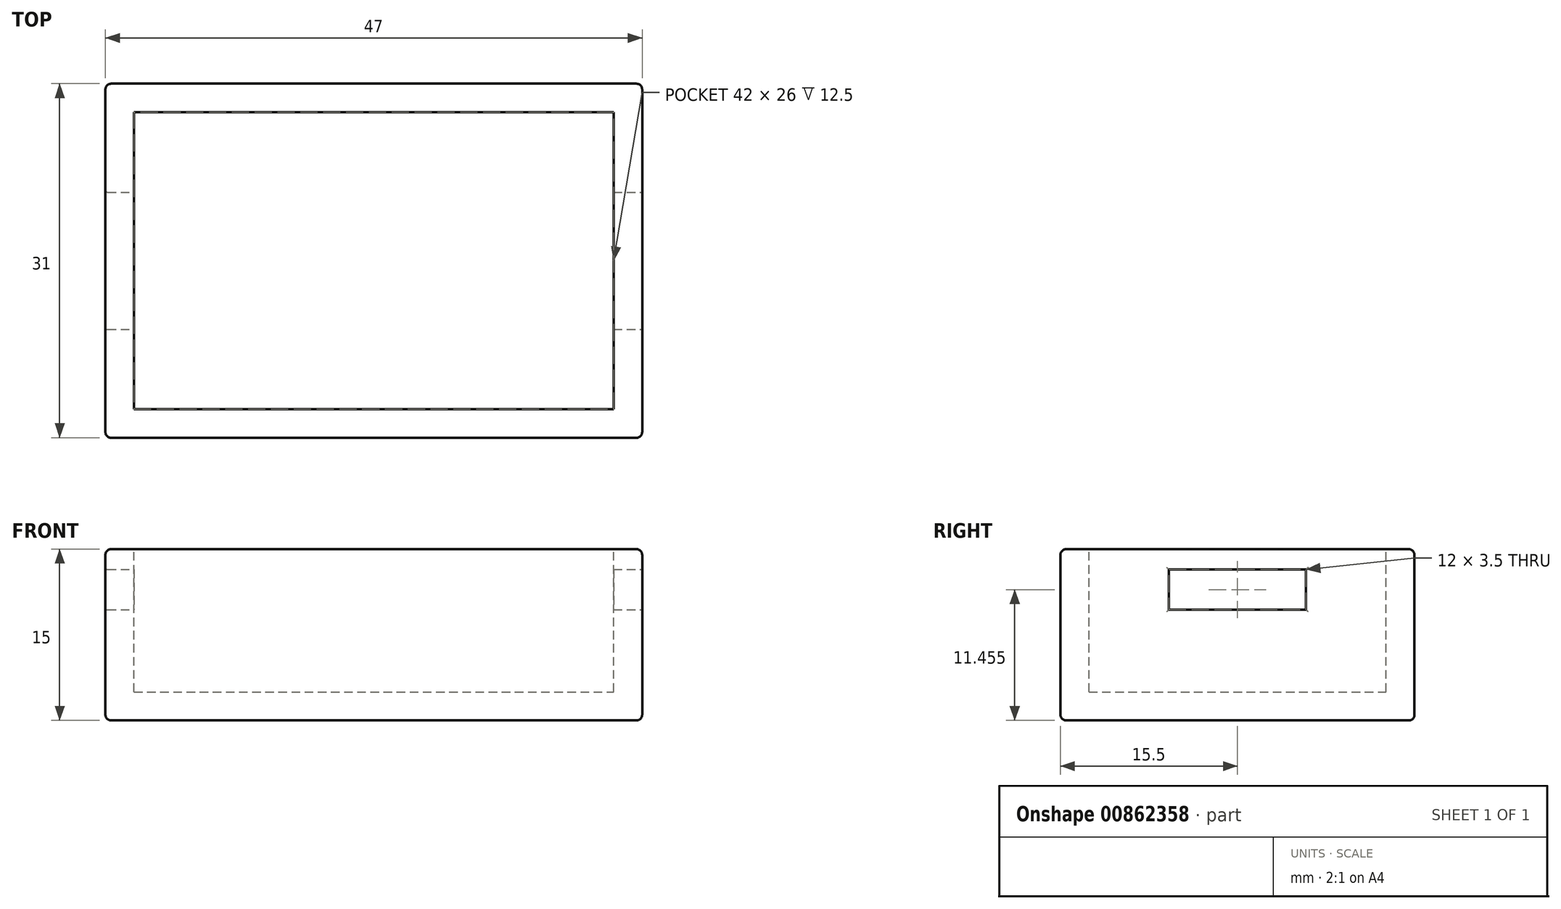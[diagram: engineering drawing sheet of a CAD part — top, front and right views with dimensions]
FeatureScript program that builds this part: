
annotation { "Feature Type Name" : "Feature", "Feature Type Description" : "" }
export const myFeature = defineFeature(function(context is Context, id is Id, definition is map)
    precondition{}
    {
        {
            var Q0;
            Q0=qCreatedBy(makeId("Front.planeOp"),FACE);
            var sketch = newSketch(context, id + "F0", { "sketchPlane" : qUnion([Q0])});
            skLineSegment(sketch, "E0.bottom", {"start": v(23.5, -7.5) * mm, "end": v(-23.5, -7.5) * mm});
            skLineSegment(sketch, "E0.top", {"start": v(23.5, 7.5) * mm, "end": v(-23.5, 7.5) * mm});
            skLineSegment(sketch, "E0.left", {"start": v(23.5, -7.5) * mm, "end": v(23.5, 7.5) * mm});
            skLineSegment(sketch, "E0.right", {"start": v(-23.5, -7.5) * mm, "end": v(-23.5, 7.5) * mm});
            skPoint(sketch, "E0.middle", {"position": v(0, 0) * mm});
            skSolve(sketch);
        }
        {
            var Q0;
            Q0=makeQuery(id+"F0.imprint","IMPRINT",FACE,{"disambiguationData":[TD([[makeQuery(id+"F0.imprint","IMPRINT",EDGE,{"derivedFrom":sQuery(id+"F0.wireOp",EDGE,"E0.bottom")}),-1.0]])]});
            extrude(context, id + "F1", {"entities" : qUnion([Q0]), "depth" : 31 * mm, "offsetDistance" : 25 * mm});
        }
        {
            var Q0;
            Q0=makeQuery(id+"F1.opExtrude","CAP_EDGE",EDGE,{"disambiguationData":[OSD([sQuery(id+"F0.wireOp",EDGE,"E0.right")])],"isStart":false});
            var Q1;
            Q1=makeQuery(id+"F1.opExtrude","CAP_EDGE",EDGE,{"disambiguationData":[OSD([sQuery(id+"F0.wireOp",EDGE,"E0.bottom")])],"isStart":false});
            var Q2;
            Q2=makeQuery(id+"F1.opExtrude","CAP_EDGE",EDGE,{"disambiguationData":[OSD([sQuery(id+"F0.wireOp",EDGE,"E0.top")])],"isStart":false});
            var Q3;
            Q3=makeQuery(id+"F1.opExtrude","CAP_EDGE",EDGE,{"disambiguationData":[OSD([sQuery(id+"F0.wireOp",EDGE,"E0.left")])],"isStart":false});
            var Q4;
            Q4=makeQuery(id+"F1.opExtrude","SWEPT_EDGE",EDGE,{"disambiguationData":[OSD([sQuery(id+"F0.wireOp",EDGE,"E0.bottom"),sQuery(id+"F0.wireOp",EDGE,"E0.left")])]});
            var Q5;
            Q5=makeQuery(id+"F1.opExtrude","CAP_EDGE",EDGE,{"disambiguationData":[OSD([sQuery(id+"F0.wireOp",EDGE,"E0.top")])],"isStart":true});
            var Q6;
            Q6=makeQuery(id+"F1.opExtrude","CAP_EDGE",EDGE,{"disambiguationData":[OSD([sQuery(id+"F0.wireOp",EDGE,"E0.left")])],"isStart":true});
            var Q7;
            Q7=makeQuery(id+"F1.opExtrude","CAP_EDGE",EDGE,{"disambiguationData":[OSD([sQuery(id+"F0.wireOp",EDGE,"E0.bottom")])],"isStart":true});
            var Q8;
            Q8=makeQuery(id+"F1.opExtrude","SWEPT_EDGE",EDGE,{"disambiguationData":[OSD([sQuery(id+"F0.wireOp",EDGE,"E0.top"),sQuery(id+"F0.wireOp",EDGE,"E0.left")])]});
            var Q9;
            Q9=makeQuery(id+"F1.opExtrude","SWEPT_EDGE",EDGE,{"disambiguationData":[OSD([sQuery(id+"F0.wireOp",EDGE,"E0.top"),sQuery(id+"F0.wireOp",EDGE,"E0.right")])]});
            var Q10;
            Q10=makeQuery(id+"F1.opExtrude","CAP_EDGE",EDGE,{"disambiguationData":[OSD([sQuery(id+"F0.wireOp",EDGE,"E0.right")])],"isStart":true});
            var Q11;
            Q11=makeQuery(id+"F1.opExtrude","SWEPT_EDGE",EDGE,{"disambiguationData":[OSD([sQuery(id+"F0.wireOp",EDGE,"E0.bottom"),sQuery(id+"F0.wireOp",EDGE,"E0.right")])]});
            fillet(context, id + "F2", {"entities" : qUnion([Q0, Q1, Q2, Q3, Q4, Q5, Q6, Q7, Q8, Q9, Q10, Q11]), "radius" : .5 * mm, "tangentPropagation" : true, "allowEdgeOverflow" : false});
        }
        {
            var Q0;
            Q0=makeQuery(id+"F1.opExtrude","SWEPT_FACE",FACE,{"disambiguationData":[OSD([sQuery(id+"F0.wireOp",EDGE,"E0.top")])]});
            var Q1;
            Q1=makeQuery(id+"F1.opExtrude","SWEPT_BODY",BODY,{"disambiguationData":[OSD([sQuery(id+"F0.wireOp",EDGE,"E0.bottom"),sQuery(id+"F0.wireOp",EDGE,"E0.top"),sQuery(id+"F0.wireOp",EDGE,"E0.left"),sQuery(id+"F0.wireOp",EDGE,"E0.right")])]});
            shell(context, id + "F3", {"entities" : qUnion([Q0]), "parts" : qUnion([Q1]), "thickness" : 2.5 * mm});
        }
        {
            var Q0;
            Q0=makeQuery(id+"F1.opExtrude","SWEPT_FACE",FACE,{"disambiguationData":[OSD([sQuery(id+"F0.wireOp",EDGE,"E0.left")])]});
            var sketch = newSketch(context, id + "F4", { "sketchPlane" : qUnion([Q0])});
            skLineSegment(sketch, "E1", {"start": v(-30.5, 3.96) * mm, "end": v(-0.5, 3.96) * mm});
            skLineSegment(sketch, "E2.bottom", {"start": v(-9.5, 2.2) * mm, "end": v(-21.5, 2.2) * mm});
            skLineSegment(sketch, "E2.top", {"start": v(-9.5, 5.7) * mm, "end": v(-21.5, 5.7) * mm});
            skLineSegment(sketch, "E2.left", {"start": v(-9.5, 2.2) * mm, "end": v(-9.5, 5.7) * mm});
            skLineSegment(sketch, "E2.right", {"start": v(-21.5, 2.2) * mm, "end": v(-21.5, 5.7) * mm});
            skPoint(sketch, "E2.middle", {"position": v(-15.5, 3.96) * mm});
            skSolve(sketch);
        }
        {
            var Q0;
            {var subQ5=sQuery(id+"F4.wireOp",EDGE,"E2.bottom");Q0=makeQuery(id+"F4.imprint","IMPRINT",FACE,{"disambiguationData":[TD([[makeQuery(id+"F4.imprint","IMPRINT",EDGE,{"derivedFrom":subQ5}),-1.0]])]});}
            var Q1;
            {var subQ5=sQuery(id+"F4.wireOp",EDGE,"E2.top");Q1=makeQuery(id+"F4.imprint","IMPRINT",FACE,{"disambiguationData":[TD([[makeQuery(id+"F4.imprint","IMPRINT",EDGE,{"derivedFrom":subQ5}),1.0]])]});}
            extrude(context, id + "F5", {"entities" : qUnion([Q0, Q1]), "operationType" : NewBodyOperationType.REMOVE, "oppositeDirection" : true, "depth" : 150 * mm, "offsetDistance" : 25 * mm});
        }
        {
            var Q0;
            Q0=makeQuery(id+"F5.boolean.opBoolean","COPY",EDGE,{"derivedFrom":makeQuery(id+"F5.opExtrude","CAP_EDGE",EDGE,{"disambiguationData":[OSD([sQuery(id+"F4.wireOp",EDGE,"E2.bottom")])],"isStart":true})});
            var Q1;
            Q1=makeQuery(id+"F5.boolean.opBoolean","COPY",EDGE,{"derivedFrom":makeQuery(id+"F5.opExtrude","CAP_EDGE",EDGE,{"disambiguationData":[OSD([sQuery(id+"F4.wireOp",EDGE,"E2.top")])],"isStart":true})});
            var Q2;
            Q2=makeQuery(id+"F5.boolean.opBoolean","COPY",EDGE,{"derivedFrom":makeQuery(id+"F5.opExtrude","CAP_EDGE",EDGE,{"disambiguationData":[OSD([sQuery(id+"F4.wireOp",EDGE,"E2.right")])],"isStart":true})});
            var Q3;
            Q3=makeQuery(id+"F5.boolean.opBoolean","COPY",EDGE,{"derivedFrom":makeQuery(id+"F5.opExtrude","CAP_EDGE",EDGE,{"disambiguationData":[OSD([sQuery(id+"F4.wireOp",EDGE,"E2.left")])],"isStart":true})});
            var Q4;
            Q4=makeQuery(id+"F5.boolean.opBoolean","INTERSECT",EDGE,{"derivedFrom":[makeQuery(id+"F1.opExtrude","SWEPT_FACE",FACE,{"disambiguationData":[OSD([sQuery(id+"F0.wireOp",EDGE,"E0.right")])]}),makeQuery(id+"F5.opExtrude","SWEPT_FACE",FACE,{"disambiguationData":[OSD([sQuery(id+"F4.wireOp",EDGE,"E2.bottom")])]})]});
            var Q5;
            Q5=makeQuery(id+"F5.boolean.opBoolean","INTERSECT",EDGE,{"derivedFrom":[makeQuery(id+"F1.opExtrude","SWEPT_FACE",FACE,{"disambiguationData":[OSD([sQuery(id+"F0.wireOp",EDGE,"E0.right")])]}),makeQuery(id+"F5.opExtrude","SWEPT_FACE",FACE,{"disambiguationData":[OSD([sQuery(id+"F4.wireOp",EDGE,"E2.top")])]})]});
            var Q6;
            Q6=makeQuery(id+"F5.boolean.opBoolean","INTERSECT",EDGE,{"derivedFrom":[makeQuery(id+"F1.opExtrude","SWEPT_FACE",FACE,{"disambiguationData":[OSD([sQuery(id+"F0.wireOp",EDGE,"E0.right")])]}),makeQuery(id+"F5.opExtrude","SWEPT_FACE",FACE,{"disambiguationData":[OSD([sQuery(id+"F4.wireOp",EDGE,"E2.left")])]})]});
            var Q7;
            Q7=makeQuery(id+"F5.boolean.opBoolean","INTERSECT",EDGE,{"derivedFrom":[makeQuery(id+"F1.opExtrude","SWEPT_FACE",FACE,{"disambiguationData":[OSD([sQuery(id+"F0.wireOp",EDGE,"E0.right")])]}),makeQuery(id+"F5.opExtrude","SWEPT_FACE",FACE,{"disambiguationData":[OSD([sQuery(id+"F4.wireOp",EDGE,"E2.right")])]})]});
            fillet(context, id + "F6", {"entities" : qUnion([Q0, Q1, Q2, Q3, Q4, Q5, Q6, Q7]), "radius" : .2 * mm, "tangentPropagation" : true, "allowEdgeOverflow" : false});
        }
    });
